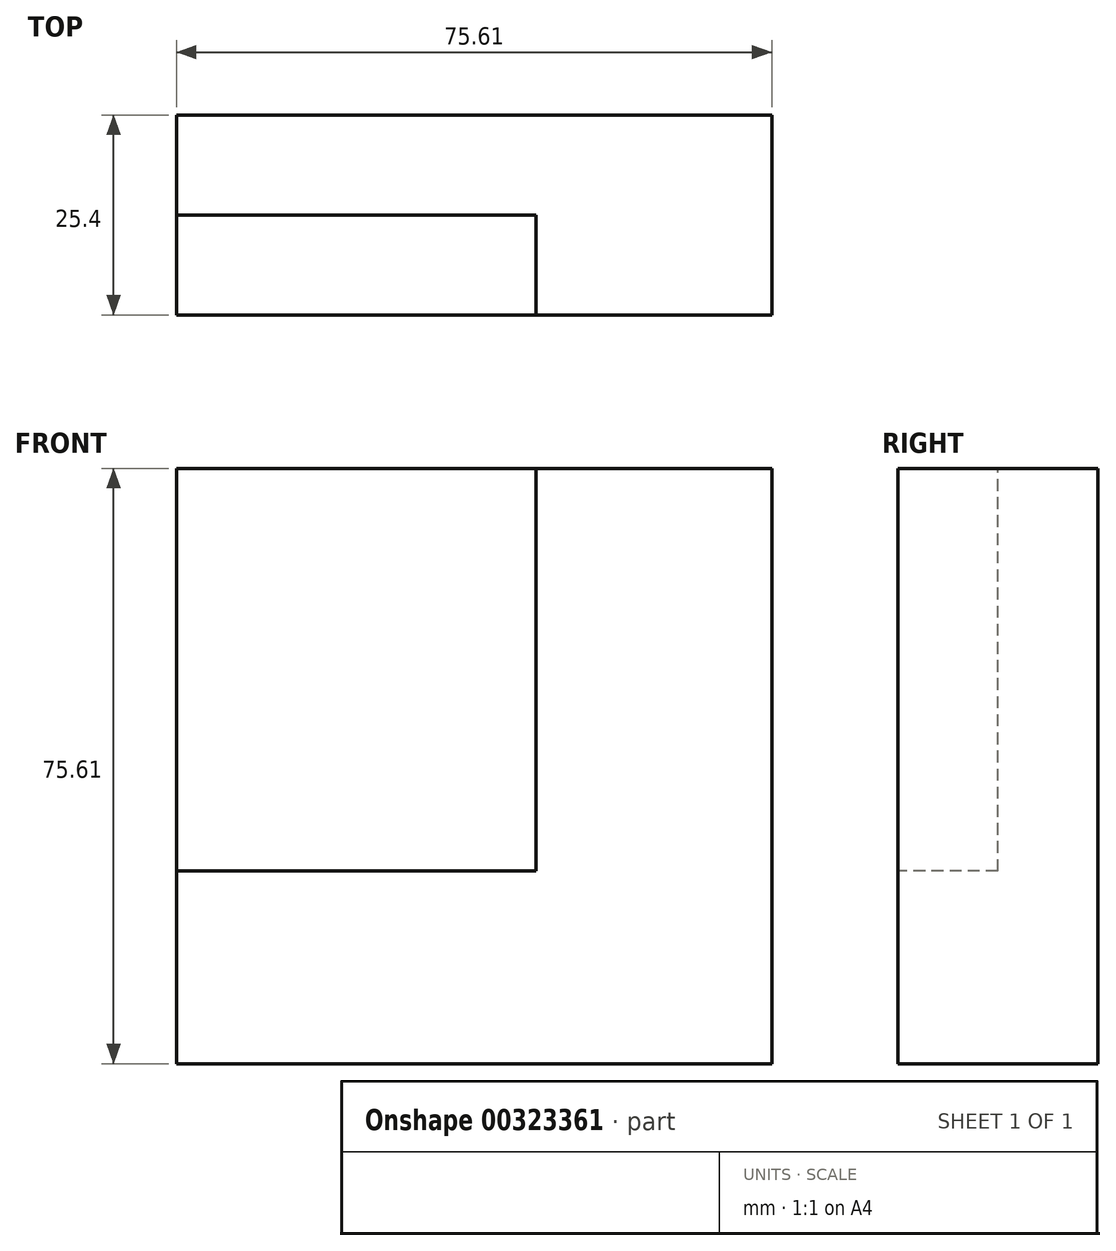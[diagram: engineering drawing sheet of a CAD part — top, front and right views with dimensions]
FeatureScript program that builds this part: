
annotation { "Feature Type Name" : "Feature", "Feature Type Description" : "" }
export const myFeature = defineFeature(function(context is Context, id is Id, definition is map)
    precondition{}
    {
        {
            var Q0;
            Q0=qCreatedBy(makeId("Front.planeOp"),FACE);
            var sketch = newSketch(context, id + "F0", { "sketchPlane" : qUnion([Q0])});
            skLineSegment(sketch, "E0", {"start": v(0, 0) * mm, "end": v(75.6, 0) * mm});
            skLineSegment(sketch, "E1", {"start": v(75.6, 0) * mm, "end": v(75.6, -75.6) * mm});
            skLineSegment(sketch, "E2", {"start": v(75.6, -75.6) * mm, "end": v(0, -75.6) * mm});
            skLineSegment(sketch, "E3", {"start": v(0, -75.6) * mm, "end": v(0, 0) * mm});
            skSolve(sketch);
        }
        {
            var Q0;
            Q0=makeQuery(id+"F0.imprint","IMPRINT",FACE,{"disambiguationData":[TD([[makeQuery(id+"F0.imprint","IMPRINT",EDGE,{"derivedFrom":sQuery(id+"F0.wireOp",EDGE,"E0")}),-1.0]])]});
            extrude(context, id + "F1", {"entities" : qUnion([Q0]), "depth" : 25.4 * mm});
        }
        {
            var Q0;
            Q0=makeQuery(id+"F1.opExtrude","CAP_FACE",FACE,{"disambiguationData":[OSD([sQuery(id+"F0.wireOp",EDGE,"E0"),sQuery(id+"F0.wireOp",EDGE,"E1"),sQuery(id+"F0.wireOp",EDGE,"E2"),sQuery(id+"F0.wireOp",EDGE,"E3")])],"isStart":false});
            var sketch = newSketch(context, id + "F2", { "sketchPlane" : qUnion([Q0])});
            skLineSegment(sketch, "E4.bottom", {"start": v(0, 0) * mm, "end": v(45.68, 0) * mm});
            skLineSegment(sketch, "E4.top", {"start": v(0, -51.14) * mm, "end": v(45.68, -51.14) * mm});
            skLineSegment(sketch, "E4.left", {"start": v(0, 0) * mm, "end": v(0, -51.14) * mm});
            skLineSegment(sketch, "E4.right", {"start": v(45.68, 0) * mm, "end": v(45.68, -51.14) * mm});
            skSolve(sketch);
        }
        {
            var Q0;
            Q0=makeQuery(id+"F2.imprint","IMPRINT",FACE,{"disambiguationData":[TD([[makeQuery(id+"F2.imprint","IMPRINT",EDGE,{"derivedFrom":sQuery(id+"F2.wireOp",EDGE,"E4.bottom")}),-1.0]])]});
            extrude(context, id + "F3", {"entities" : qUnion([Q0]), "operationType" : NewBodyOperationType.REMOVE, "oppositeDirection" : true, "depth" : 12.7 * mm});
        }
    });
